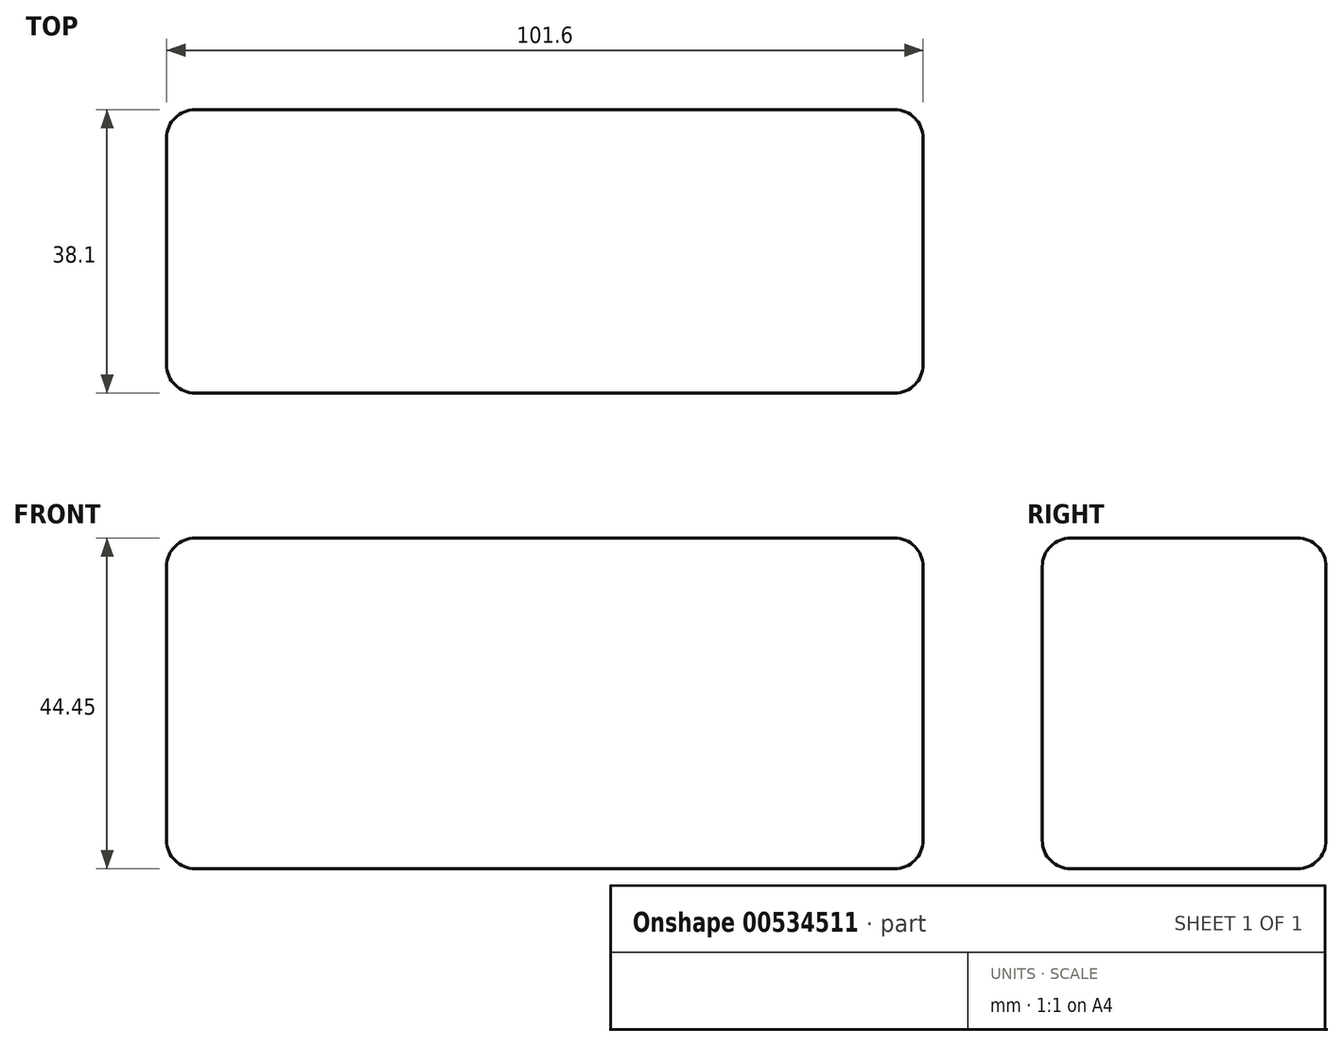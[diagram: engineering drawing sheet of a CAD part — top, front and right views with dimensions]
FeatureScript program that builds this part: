
annotation { "Feature Type Name" : "Feature", "Feature Type Description" : "" }
export const myFeature = defineFeature(function(context is Context, id is Id, definition is map)
    precondition{}
    {
        {
            var Q0;
            Q0=qCreatedBy(makeId("Front.planeOp"),FACE);
            var sketch = newSketch(context, id + "F0", { "sketchPlane" : qUnion([Q0])});
            skLineSegment(sketch, "E0.bottom", {"start": v(-43.06, 21.56) * mm, "end": v(50.92, 21.56) * mm});
            skLineSegment(sketch, "E0.top", {"start": v(-43.06, -22.9) * mm, "end": v(50.92, -22.9) * mm});
            skLineSegment(sketch, "E0.left", {"start": v(-46.87, 17.75) * mm, "end": v(-46.87, -19.08) * mm});
            skLineSegment(sketch, "E0.right", {"start": v(54.73, 17.75) * mm, "end": v(54.73, -19.08) * mm});
            skPoint(sketch, "E1.visualSharp", {"position": v(-46.87, 21.56) * mm});
            skArc(sketch, "E1.filletArc", {"start": v(-43.06, 21.56) * mm, "mid": v(-45.76, 20.44) * mm, "end": v(-46.87, 17.75) * mm});
            skPoint(sketch, "E2.visualSharp", {"position": v(-46.87, -22.9) * mm});
            skArc(sketch, "E2.filletArc", {"start": v(-46.87, -19.08) * mm, "mid": v(-45.76, -21.77) * mm, "end": v(-43.06, -22.9) * mm});
            skPoint(sketch, "E3.visualSharp", {"position": v(54.73, 21.56) * mm});
            skArc(sketch, "E3.filletArc", {"start": v(54.73, 17.75) * mm, "mid": v(53.61, 20.44) * mm, "end": v(50.92, 21.56) * mm});
            skPoint(sketch, "E4.visualSharp", {"position": v(54.73, -22.9) * mm});
            skArc(sketch, "E4.filletArc", {"start": v(50.92, -22.9) * mm, "mid": v(53.61, -21.77) * mm, "end": v(54.73, -19.08) * mm});
            skSolve(sketch);
        }
        {
            var Q0;
            Q0=makeQuery(id+"F0.imprint","IMPRINT",FACE,{"disambiguationData":[TD([[makeQuery(id+"F0.imprint","IMPRINT",EDGE,{"derivedFrom":sQuery(id+"F0.wireOp",EDGE,"E0.bottom")}),-1.0]])]});
            extrude(context, id + "F1", {"entities" : qUnion([Q0]), "depth" : 38.1 * mm, "offsetDistance" : 25.4 * mm});
        }
        {
            var Q0;
            Q0=makeQuery(id+"F1.opExtrude","CAP_EDGE",EDGE,{"disambiguationData":[OSD([sQuery(id+"F0.wireOp",EDGE,"E0.bottom")])],"isStart":false});
            var Q1;
            Q1=makeQuery(id+"F1.opExtrude","CAP_EDGE",EDGE,{"disambiguationData":[OSD([sQuery(id+"F0.wireOp",EDGE,"E0.bottom")])],"isStart":true});
            fillet(context, id + "F2", {"entities" : qUnion([Q0, Q1]), "radius" : 3.8 * mm, "tangentPropagation" : true, "allowEdgeOverflow" : false});
        }
    });
